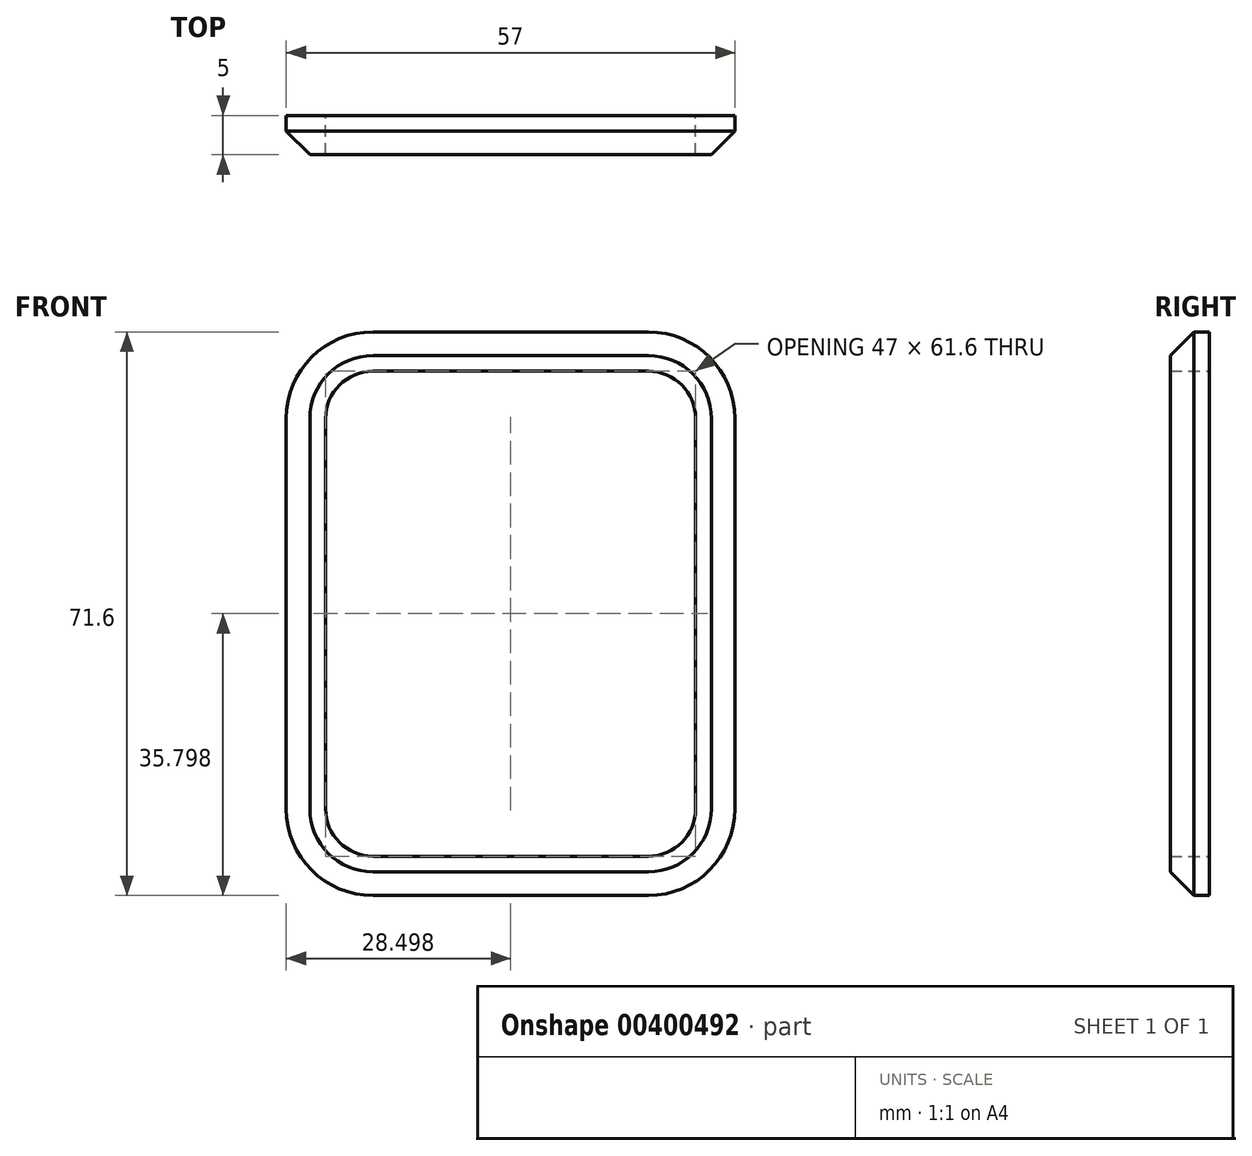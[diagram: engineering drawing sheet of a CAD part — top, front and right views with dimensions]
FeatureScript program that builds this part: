
annotation { "Feature Type Name" : "Feature", "Feature Type Description" : "" }
export const myFeature = defineFeature(function(context is Context, id is Id, definition is map)
    precondition{}
    {
        {
            var Q0;
            Q0=qCreatedBy(makeId("Front.planeOp"),FACE);
            var sketch = newSketch(context, id + "F0", { "sketchPlane" : qUnion([Q0])});
            skPoint(sketch, "E0.middle", {"position": v(-0.2, 0.29) * mm});
            skLineSegment(sketch, "E1.0", {"start": v(-17.7, 31.09) * mm, "end": v(17.3, 31.09) * mm});
            skArc(sketch, "E1.1", {"start": v(23.3, 25.09) * mm, "mid": v(21.55, 29.33) * mm, "end": v(17.3, 31.09) * mm});
            skArc(sketch, "E1.2", {"start": v(-17.7, 31.09) * mm, "mid": v(-21.93, 29.33) * mm, "end": v(-23.7, 25.09) * mm});
            skLineSegment(sketch, "E1.3", {"start": v(23.3, 25.09) * mm, "end": v(23.3, -24.51) * mm});
            skLineSegment(sketch, "E1.4", {"start": v(-23.7, 25.09) * mm, "end": v(-23.7, -24.51) * mm});
            skArc(sketch, "E1.5", {"start": v(-23.7, -24.51) * mm, "mid": v(-21.93, -28.75) * mm, "end": v(-17.7, -30.51) * mm});
            skLineSegment(sketch, "E1.6", {"start": v(-17.7, -30.51) * mm, "end": v(17.3, -30.51) * mm});
            skArc(sketch, "E1.7", {"start": v(17.3, -30.51) * mm, "mid": v(21.55, -28.75) * mm, "end": v(23.3, -24.51) * mm});
            skArc(sketch, "E2.0", {"start": v(-17.7, 36.09) * mm, "mid": v(-25.47, 32.87) * mm, "end": v(-28.7, 25.09) * mm});
            skLineSegment(sketch, "E2.1", {"start": v(-28.7, 25.09) * mm, "end": v(-28.7, -24.51) * mm});
            skLineSegment(sketch, "E2.2", {"start": v(-17.7, 36.09) * mm, "end": v(17.3, 36.09) * mm});
            skArc(sketch, "E2.3", {"start": v(-28.7, -24.51) * mm, "mid": v(-25.47, -32.29) * mm, "end": v(-17.7, -35.51) * mm});
            skArc(sketch, "E2.4", {"start": v(28.3, 25.09) * mm, "mid": v(25.09, 32.87) * mm, "end": v(17.3, 36.09) * mm});
            skLineSegment(sketch, "E2.5", {"start": v(28.3, 25.09) * mm, "end": v(28.3, -24.51) * mm});
            skArc(sketch, "E2.6", {"start": v(17.3, -35.51) * mm, "mid": v(25.09, -32.29) * mm, "end": v(28.3, -24.51) * mm});
            skLineSegment(sketch, "E2.7", {"start": v(-17.7, -35.51) * mm, "end": v(17.3, -35.51) * mm});
            skSolve(sketch);
        }
        {
            var Q0;
            Q0 = qSketchRegion(id + "F0", true);
            extrude(context, id + "F1", {"entities" : qUnion([Q0]), "depth" : 5 * mm});
        }
        {
            var Q0;
            Q0=makeQuery(id+"F1.opExtrude","CAP_EDGE",EDGE,{"disambiguationData":[OSD([sQuery(id+"F0.wireOp",EDGE,"E2.5")])],"isStart":false});
            chamfer(context, id + "F2", {"entities" : qUnion([Q0]), "width" : 3 * mm, "tangentPropagation" : true});
        }
    });
